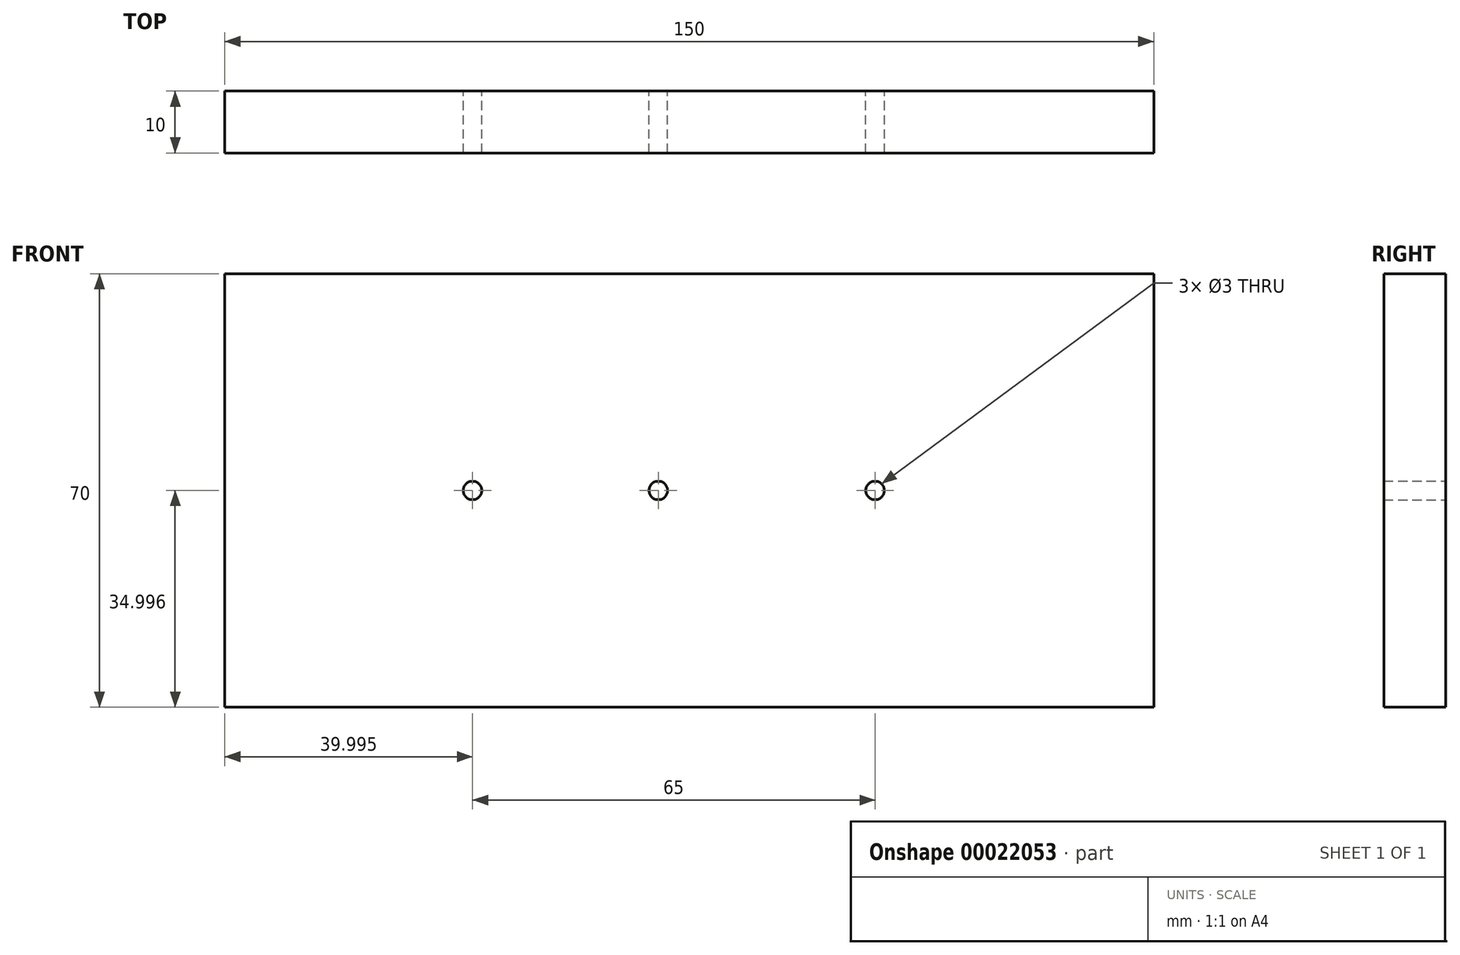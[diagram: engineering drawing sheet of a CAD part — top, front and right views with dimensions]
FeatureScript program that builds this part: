
annotation { "Feature Type Name" : "Feature", "Feature Type Description" : "" }
export const myFeature = defineFeature(function(context is Context, id is Id, definition is map)
    precondition{}
    {
        {
            var Q0;
            Q0=qCreatedBy(makeId("Front.planeOp"),FACE);
            var sketch = newSketch(context, id + "F0", { "sketchPlane" : qUnion([Q0])});
            skLineSegment(sketch, "E0.bottom", {"start": v(-44.46, 39.9) * mm, "end": v(105.54, 39.9) * mm});
            skLineSegment(sketch, "E0.top", {"start": v(-44.46, -30.1) * mm, "end": v(105.54, -30.1) * mm});
            skLineSegment(sketch, "E0.left", {"start": v(-44.46, 39.9) * mm, "end": v(-44.46, -30.1) * mm});
            skLineSegment(sketch, "E0.right", {"start": v(105.54, 39.9) * mm, "end": v(105.54, -30.1) * mm});
            skLineSegment(sketch, "E1", {"start": v(-44.46, 4.9) * mm, "end": v(-4.46, 4.9) * mm});
            skLineSegment(sketch, "E2", {"start": v(-4.46, 4.9) * mm, "end": v(25.54, 4.9) * mm});
            skLineSegment(sketch, "E3", {"start": v(25.54, 4.9) * mm, "end": v(60.54, 4.9) * mm});
            skCircle(sketch, "E4", {"center": v(-4.46, 4.9) * mm, "radius": 1.5 * mm});
            skCircle(sketch, "E5", {"center": v(25.54, 4.9) * mm, "radius": 1.5 * mm});
            skCircle(sketch, "E6", {"center": v(60.54, 4.9) * mm, "radius": 1.5 * mm});
            skSolve(sketch);
        }
        {
            var Q0;
            {var subQ10=sQuery(id+"F0.wireOp",EDGE,"E0.bottom");Q0=makeQuery(id+"F0.imprint","IMPRINT",FACE,{"disambiguationData":[TD([[makeQuery(id+"F0.imprint","IMPRINT",EDGE,{"derivedFrom":subQ10}),-1.0]])]});}
            extrude(context, id + "F1", {"entities" : qUnion([Q0]), "depth" : 10 * mm});
        }
    });
